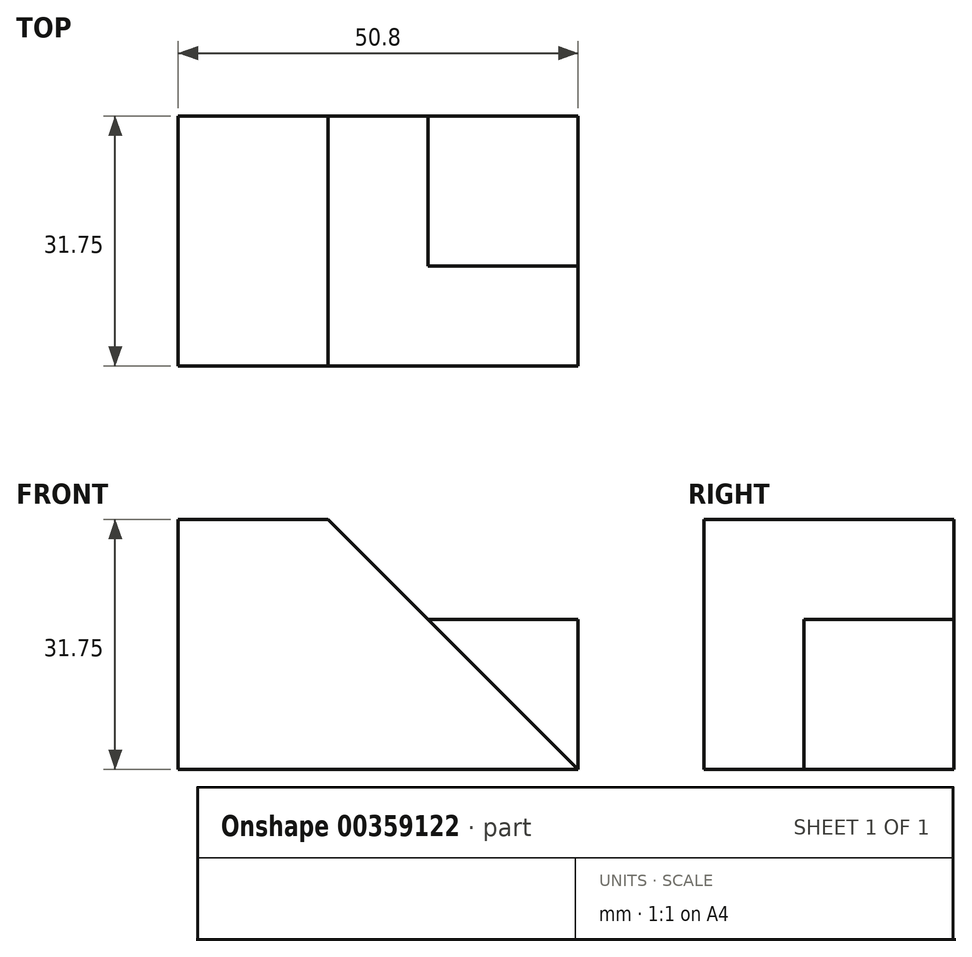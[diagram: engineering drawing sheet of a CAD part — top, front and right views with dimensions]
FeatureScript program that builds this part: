
annotation { "Feature Type Name" : "Feature", "Feature Type Description" : "" }
export const myFeature = defineFeature(function(context is Context, id is Id, definition is map)
    precondition{}
    {
        {
            var Q0;
            Q0=qCreatedBy(makeId("Right.planeOp"),FACE);
            var sketch = newSketch(context, id + "F0", { "sketchPlane" : qUnion([Q0])});
            skLineSegment(sketch, "E0.bottom", {"start": v(0, 31.75) * mm, "end": v(31.75, 31.75) * mm});
            skLineSegment(sketch, "E0.top", {"start": v(0, 0) * mm, "end": v(31.75, 0) * mm});
            skLineSegment(sketch, "E0.left", {"start": v(0, 31.75) * mm, "end": v(0, 0) * mm});
            skLineSegment(sketch, "E0.right", {"start": v(31.75, 31.75) * mm, "end": v(31.75, 0) * mm});
            skSolve(sketch);
        }
        {
            var Q0;
            Q0=makeQuery(id+"F0.imprint","IMPRINT",FACE,{"disambiguationData":[TD([[makeQuery(id+"F0.imprint","IMPRINT",EDGE,{"derivedFrom":sQuery(id+"F0.wireOp",EDGE,"E0.bottom")}),-1.0]])]});
            extrude(context, id + "F1", {"entities" : qUnion([Q0]), "depth" : 50.8 * mm});
        }
        {
            var Q0;
            Q0=makeQuery(id+"F1.opExtrude","SWEPT_FACE",FACE,{"disambiguationData":[OSD([sQuery(id+"F0.wireOp",EDGE,"E0.left")])]});
            var sketch = newSketch(context, id + "F2", { "sketchPlane" : qUnion([Q0])});
            skLineSegment(sketch, "E1", {"start": v(50.8, 0) * mm, "end": v(19.05, 31.75) * mm});
            skSolve(sketch);
        }
        {
            var Q0;
            {var subQ0=sQuery(id+"F2.wireOp",EDGE,"E1");Q0=makeQuery(id+"F2.imprint","IMPRINT",FACE,{"disambiguationData":[TD([[makeQuery(id+"F2.imprint","IMPRINT",EDGE,{"derivedFrom":subQ0}),-1.0]])]});}
            extrude(context, id + "F3", {"entities" : qUnion([Q0]), "operationType" : NewBodyOperationType.REMOVE, "oppositeDirection" : true, "depth" : 12.7 * mm});
        }
        {
            var Q0;
            Q0=makeQuery(id+"F3.boolean.opBoolean","COPY",FACE,{"derivedFrom":makeQuery(id+"F3.opExtrude","CAP_FACE",FACE,{"disambiguationData":[OSD([sQuery(id+"F0.wireOp",EDGE,"E0.bottom"),sQuery(id+"F0.wireOp",EDGE,"E0.left"),sQuery(id+"F2.wireOp",EDGE,"E1")])],"isStart":false})});
            var sketch = newSketch(context, id + "F4", { "sketchPlane" : qUnion([Q0])});
            skLineSegment(sketch, "E2", {"start": v(31.75, 19.05) * mm, "end": v(50.8, 19.05) * mm});
            skSolve(sketch);
        }
        {
            var Q0;
            {var subQ0=sQuery(id+"F4.wireOp",EDGE,"E2");Q0=makeQuery(id+"F4.imprint","IMPRINT",FACE,{"disambiguationData":[TD([[makeQuery(id+"F4.imprint","IMPRINT",EDGE,{"derivedFrom":subQ0}),1.0]])]});}
            extrude(context, id + "F5", {"entities" : qUnion([Q0]), "operationType" : NewBodyOperationType.REMOVE, "oppositeDirection" : true, "depth" : 19.05 * mm});
        }
    });
